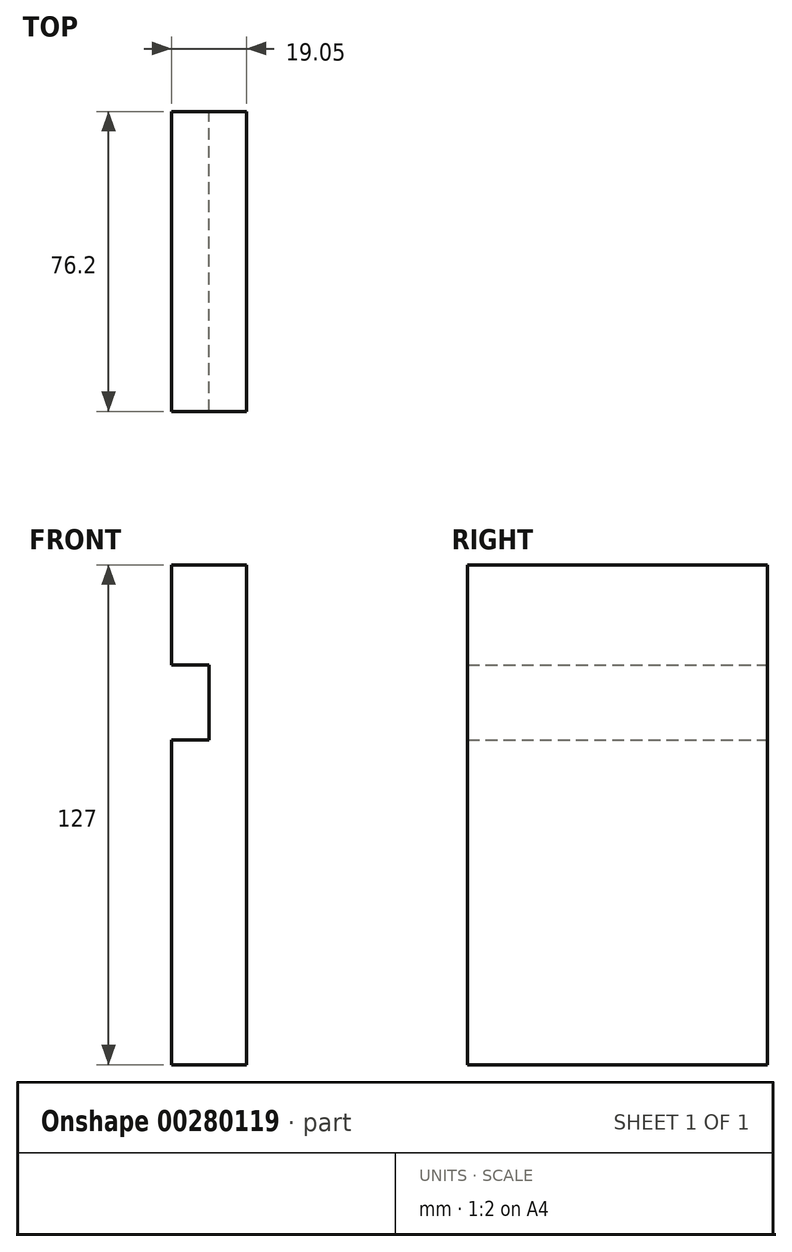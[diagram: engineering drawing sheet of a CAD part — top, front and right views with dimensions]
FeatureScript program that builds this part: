
annotation { "Feature Type Name" : "Feature", "Feature Type Description" : "" }
export const myFeature = defineFeature(function(context is Context, id is Id, definition is map)
    precondition{}
    {
        {
            var Q0;
            Q0=qCreatedBy(makeId("Front.planeOp"),FACE);
            var sketch = newSketch(context, id + "F0", { "sketchPlane" : qUnion([Q0])});
            skLineSegment(sketch, "E0", {"start": v(-11.13, 50.8) * mm, "end": v(-11.13, -76.2) * mm});
            skLineSegment(sketch, "E1", {"start": v(-11.13, 50.8) * mm, "end": v(-30.18, 50.8) * mm});
            skLineSegment(sketch, "E2", {"start": v(-30.18, 50.8) * mm, "end": v(-30.18, 25.4) * mm});
            skLineSegment(sketch, "E3", {"start": v(-30.18, 25.4) * mm, "end": v(-20.66, 25.4) * mm});
            skLineSegment(sketch, "E4", {"start": v(-20.66, 25.4) * mm, "end": v(-20.66, 6.34) * mm});
            skLineSegment(sketch, "E5", {"start": v(-20.66, 6.34) * mm, "end": v(-30.18, 6.34) * mm});
            skLineSegment(sketch, "E6", {"start": v(-30.18, 6.34) * mm, "end": v(-30.18, -76.2) * mm});
            skLineSegment(sketch, "E7", {"start": v(-30.18, -76.2) * mm, "end": v(-11.13, -76.2) * mm});
            skSolve(sketch);
        }
        {
            var Q0;
            Q0 = qSketchRegion(id + "F0", true);
            extrude(context, id + "F1", {"entities" : qUnion([Q0]), "depth" : 76.2 * mm});
        }
    });
